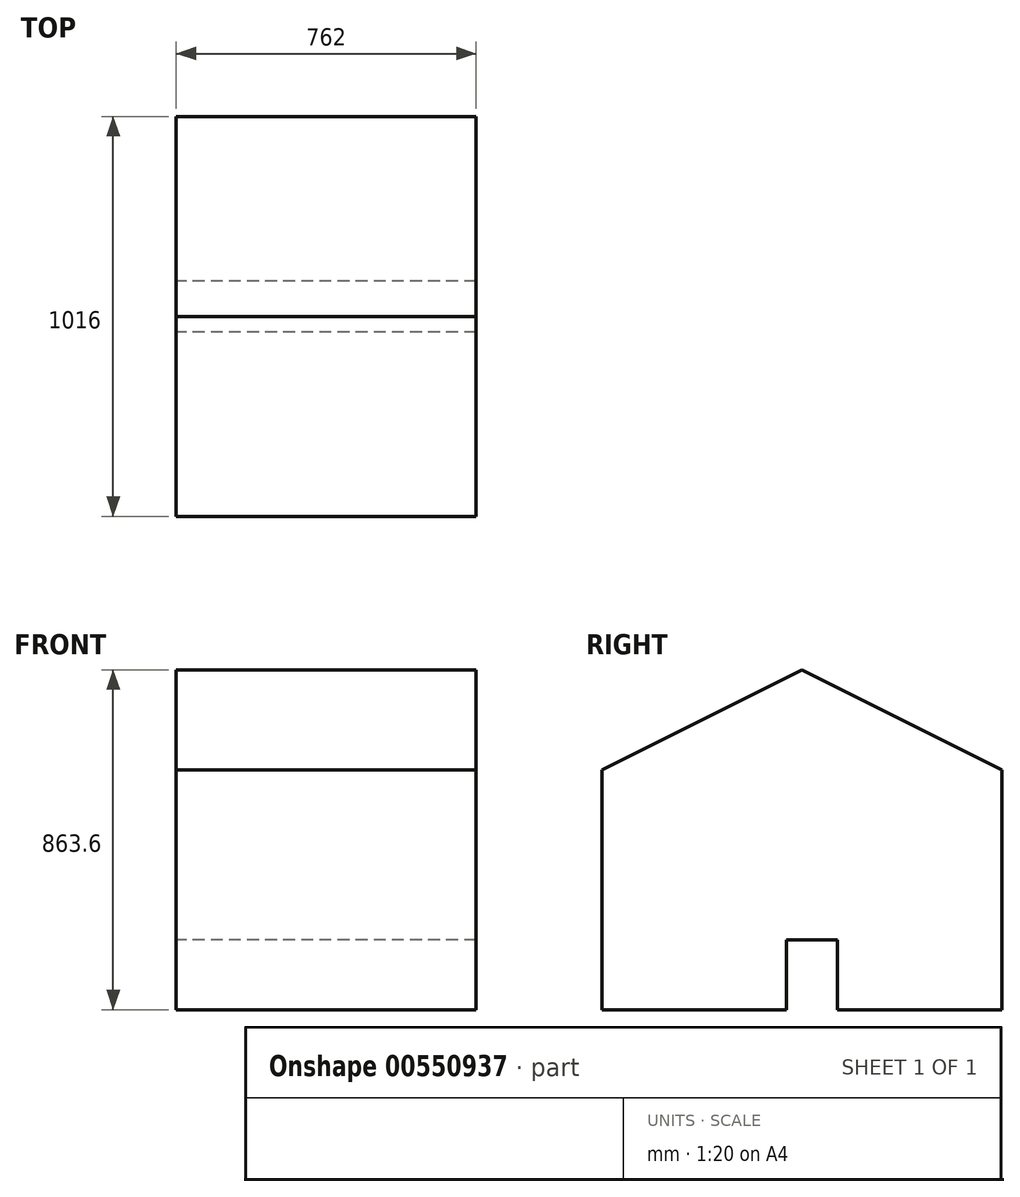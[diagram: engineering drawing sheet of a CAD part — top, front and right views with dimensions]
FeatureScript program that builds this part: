
annotation { "Feature Type Name" : "Feature", "Feature Type Description" : "" }
export const myFeature = defineFeature(function(context is Context, id is Id, definition is map)
    precondition{}
    {
        {
            var Q0;
            Q0=qCreatedBy(makeId("Right.planeOp"),FACE);
            var sketch = newSketch(context, id + "F0", { "sketchPlane" : qUnion([Q0])});
            skLineSegment(sketch, "E0", {"start": v(0, 0) * mm, "end": v(-508, 0) * mm});
            skLineSegment(sketch, "E1", {"start": v(0, 0) * mm, "end": v(508, 0) * mm});
            skLineSegment(sketch, "E2", {"start": v(0, 0) * mm, "end": v(0, 254) * mm});
            skLineSegment(sketch, "E3", {"start": v(-508, 0) * mm, "end": v(0, 254) * mm});
            skLineSegment(sketch, "E4", {"start": v(0, 254) * mm, "end": v(508, 0) * mm});
            skLineSegment(sketch, "E5", {"start": v(-508, 0) * mm, "end": v(-508, -609.6) * mm});
            skLineSegment(sketch, "E6", {"start": v(508, 0) * mm, "end": v(508, -609.6) * mm});
            skLineSegment(sketch, "E7", {"start": v(-508, -609.6) * mm, "end": v(508, -609.6) * mm});
            skLineSegment(sketch, "E8", {"start": v(0, 254) * mm, "end": v(0, 292.1) * mm});
            skLineSegment(sketch, "E9", {"start": v(0, 292.1) * mm, "end": v(-566.12, 0) * mm});
            skLineSegment(sketch, "E10", {"start": v(0, 292.1) * mm, "end": v(584.2, 0) * mm});
            skLineSegment(sketch, "E11", {"start": v(-508, 0) * mm, "end": v(-566.12, 0) * mm});
            skLineSegment(sketch, "E12.bottom", {"start": v(-40.12, -609.6) * mm, "end": v(89.25, -609.6) * mm});
            skLineSegment(sketch, "E12.top", {"start": v(-40.12, -431.8) * mm, "end": v(89.25, -431.8) * mm});
            skLineSegment(sketch, "E12.left", {"start": v(-40.12, -609.6) * mm, "end": v(-40.12, -431.8) * mm});
            skLineSegment(sketch, "E12.right", {"start": v(89.25, -609.6) * mm, "end": v(89.25, -431.8) * mm});
            skLineSegment(sketch, "E13.bottom", {"start": v(-355.6, -177.8) * mm, "end": v(-177.8, -177.8) * mm});
            skLineSegment(sketch, "E13.top", {"start": v(-355.6, -355.6) * mm, "end": v(-177.8, -355.6) * mm});
            skLineSegment(sketch, "E13.left", {"start": v(-355.6, -177.8) * mm, "end": v(-355.6, -355.6) * mm});
            skLineSegment(sketch, "E13.right", {"start": v(-177.8, -177.8) * mm, "end": v(-177.8, -355.6) * mm});
            skLineSegment(sketch, "E14.bottom", {"start": v(50.8, -76.2) * mm, "end": v(457.2, -76.2) * mm});
            skLineSegment(sketch, "E14.top", {"start": v(50.8, -279.4) * mm, "end": v(457.2, -279.4) * mm});
            skLineSegment(sketch, "E14.left", {"start": v(50.8, -76.2) * mm, "end": v(50.8, -279.4) * mm});
            skLineSegment(sketch, "E14.right", {"start": v(457.2, -76.2) * mm, "end": v(457.2, -279.4) * mm});
            skSolve(sketch);
        }
        {
            var Q0;
            Q0=makeQuery(id+"F0.imprint","IMPRINT",FACE,{"disambiguationData":[TD([[makeQuery(id+"F0.imprint","IMPRINT",EDGE,{"derivedFrom":sQuery(id+"F0.wireOp",EDGE,"E13.bottom")}),-1.0]])]});
            var Q1;
            Q1=makeQuery(id+"F0.imprint","IMPRINT",FACE,{"disambiguationData":[TD([[makeQuery(id+"F0.imprint","IMPRINT",EDGE,{"derivedFrom":sQuery(id+"F0.wireOp",EDGE,"E14.bottom")}),-1.0]])]});
            var Q2;
            Q2=makeQuery(id+"F0.imprint","IMPRINT",FACE,{"disambiguationData":[TD([[makeQuery(id+"F0.imprint","IMPRINT",EDGE,{"derivedFrom":sQuery(id+"F0.wireOp",EDGE,"E12.bottom")}),1.0]])]});
            var Q3;
            Q3=makeQuery(id+"F0.imprint","IMPRINT",FACE,{"disambiguationData":[TD([[makeQuery(id+"F0.imprint","IMPRINT",EDGE,{"derivedFrom":sQuery(id+"F0.wireOp",EDGE,"E0")}),-1.0]])]});
            var Q4;
            Q4=makeQuery(id+"F0.imprint","IMPRINT",FACE,{"disambiguationData":[TD([[makeQuery(id+"F0.imprint","IMPRINT",EDGE,{"derivedFrom":sQuery(id+"F0.wireOp",EDGE,"E1")}),1.0]])]});
            var Q5;
            Q5=makeQuery(id+"F0.imprint","IMPRINT",FACE,{"disambiguationData":[TD([[makeQuery(id+"F0.imprint","IMPRINT",EDGE,{"derivedFrom":sQuery(id+"F0.wireOp",EDGE,"E0")}),1.0]])]});
            extrude(context, id + "F1", {"entities" : qUnion([Q0, Q1, Q2, Q3, Q4, Q5]), "depth" : 762 * mm, "offsetDistance" : 25.4 * mm});
        }
    });
